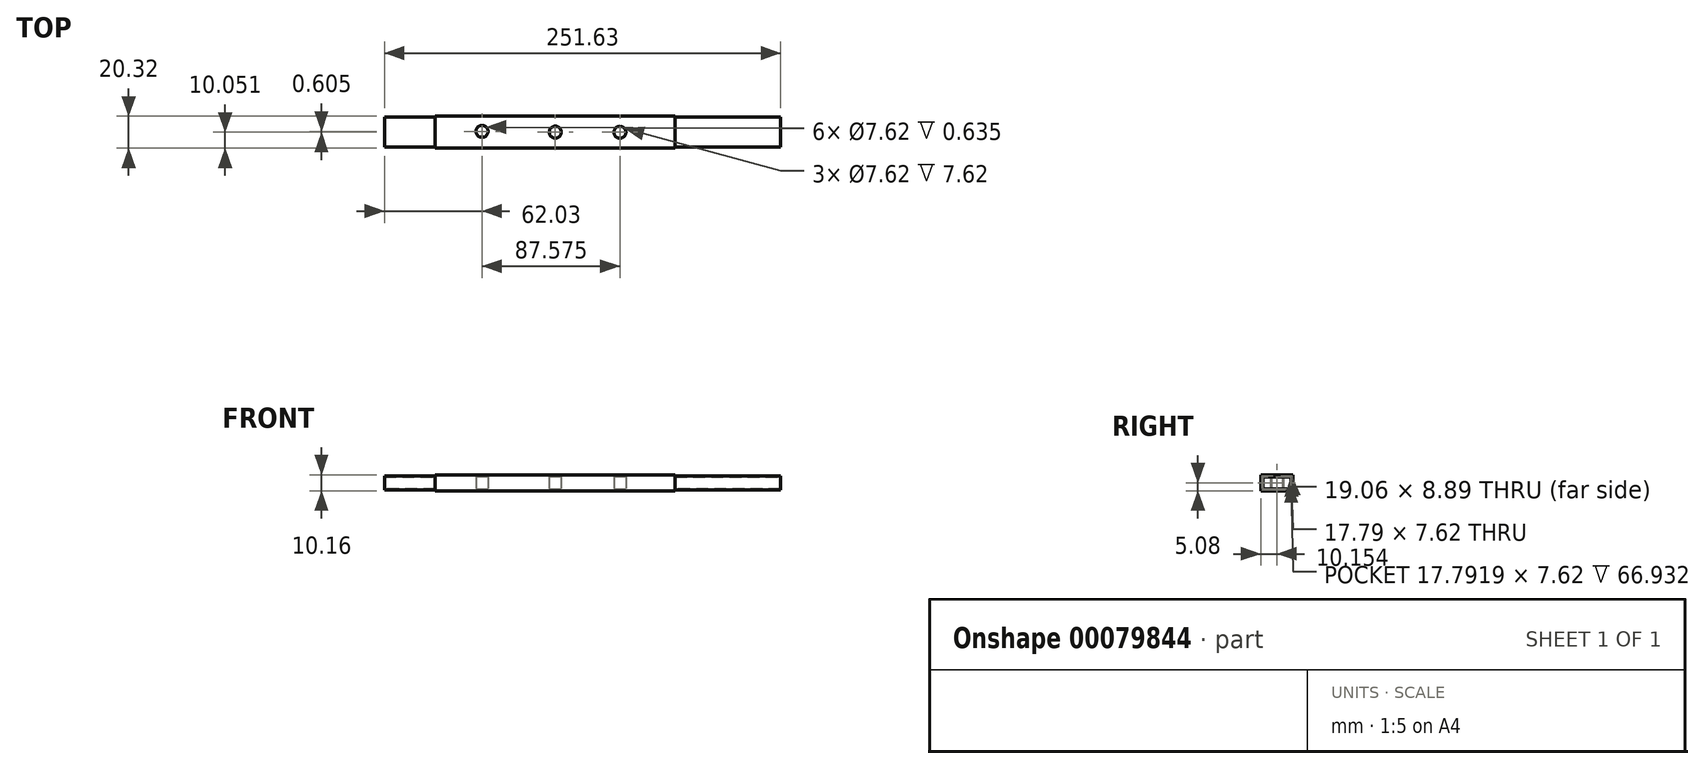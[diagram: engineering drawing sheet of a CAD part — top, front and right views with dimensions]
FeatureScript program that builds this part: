
annotation { "Feature Type Name" : "Feature", "Feature Type Description" : "" }
export const myFeature = defineFeature(function(context is Context, id is Id, definition is map)
    precondition{}
    {
        {
            var Q0;
            Q0=qCreatedBy(makeId("Top.planeOp"),FACE);
            var sketch = newSketch(context, id + "F0", { "sketchPlane" : qUnion([Q0])});
            skLineSegment(sketch, "E0.bottom", {"start": v(76.2, -10.16) * mm, "end": v(-76.2, -10.16) * mm});
            skLineSegment(sketch, "E0.top", {"start": v(76.2, 10.16) * mm, "end": v(-76.2, 10.16) * mm});
            skLineSegment(sketch, "E0.left", {"start": v(76.2, -10.16) * mm, "end": v(76.2, 10.16) * mm});
            skLineSegment(sketch, "E0.right", {"start": v(-76.2, -10.16) * mm, "end": v(-76.2, 10.16) * mm});
            skPoint(sketch, "E0.middle", {"position": v(0, 0) * mm});
            skCircle(sketch, "E1", {"center": v(0, 0) * mm, "radius": 3.81 * mm});
            skPoint(sketch, "E2.middle", {"position": v(-46.47, 0.5) * mm});
            skCircle(sketch, "E3", {"center": v(-46.47, 0.5) * mm, "radius": 3.81 * mm});
            skPoint(sketch, "E4.middle", {"position": v(41.1, -0.1) * mm});
            skCircle(sketch, "E5", {"center": v(41.1, -0.1) * mm, "radius": 3.81 * mm});
            skSolve(sketch);
        }
        {
            var Q0;
            Q0=makeQuery(id+"F0.imprint","IMPRINT",FACE,{"disambiguationData":[TD([[makeQuery(id+"F0.imprint","IMPRINT",EDGE,{"derivedFrom":sQuery(id+"F0.wireOp",EDGE,"E0.bottom")}),-1.0]])]});
            var Q1;
            Q1 = qSketchRegion(id + "F2", true);
            extrude(context, id + "F1", {"entities" : qUnion([Q0, Q1]), "depth" : 10.16 * mm});
        }
        {
            var Q0;
            Q0=makeQuery(id+"F1.opExtrude","SWEPT_FACE",FACE,{"disambiguationData":[OSD([sQuery(id+"F0.wireOp",EDGE,"E0.left")])]});
            var sketch = newSketch(context, id + "F2", { "sketchPlane" : qUnion([Q0])});
            skLineSegment(sketch, "E6.bottom", {"start": v(-9.54, 9.53) * mm, "end": v(9.53, 9.53) * mm});
            skLineSegment(sketch, "E6.top", {"start": v(-9.54, 0.64) * mm, "end": v(9.53, 0.64) * mm});
            skLineSegment(sketch, "E6.left", {"start": v(-9.54, 9.53) * mm, "end": v(-9.54, 0.64) * mm});
            skLineSegment(sketch, "E6.right", {"start": v(9.53, 9.53) * mm, "end": v(9.53, 0.64) * mm});
            skSolve(sketch);
        }
        {
            var Q0;
            Q0=sQuery(id+"F2.wireOp",EDGE,"E6.left");
            var Q1;
            Q1=sQuery(id+"F2.wireOp",EDGE,"E6.bottom");
            var Q2;
            Q2=sQuery(id+"F2.wireOp",EDGE,"E6.top");
            var Q3;
            Q3=sQuery(id+"F2.wireOp",EDGE,"E6.right");
            extrude(context, id + "F3", {"bodyType" : ToolBodyType.SURFACE, "surfaceEntities" : qUnion([Q0, Q1, Q2, Q3]), "depth" : 66.93 * mm, "hasSecondDirection" : true, "secondDirectionOppositeDirection" : true, "secondDirectionDepth" : 184.7 * mm});
        }
        {
            var Q0;
            Q0=makeQuery(id+"F3.opExtrude","SWEPT_FACE",FACE,{"disambiguationData":[OSD([sQuery(id+"F2.wireOp",EDGE,"E6.right")])]});
            extrude(context, id + "F4", {"entities" : qUnion([Q0]), "oppositeDirection" : true, "depth" : 0.64 * mm});
        }
        {
            var Q0;
            Q0=makeQuery(id+"F3.opExtrude","SWEPT_FACE",FACE,{"disambiguationData":[OSD([sQuery(id+"F2.wireOp",EDGE,"E6.bottom")])]});
            extrude(context, id + "F5", {"entities" : qUnion([Q0]), "operationType" : NewBodyOperationType.ADD, "oppositeDirection" : true, "depth" : 0.64 * mm});
        }
        {
            var Q0;
            Q0=makeQuery(id+"F3.opExtrude","SWEPT_FACE",FACE,{"disambiguationData":[OSD([sQuery(id+"F2.wireOp",EDGE,"E6.left")])]});
            extrude(context, id + "F6", {"entities" : qUnion([Q0]), "operationType" : NewBodyOperationType.ADD, "oppositeDirection" : true, "depth" : 0.64 * mm});
        }
        {
            var Q0;
            Q0=makeQuery(id+"F3.opExtrude","SWEPT_FACE",FACE,{"disambiguationData":[OSD([sQuery(id+"F2.wireOp",EDGE,"E6.top")])]});
            extrude(context, id + "F7", {"entities" : qUnion([Q0]), "operationType" : NewBodyOperationType.ADD, "oppositeDirection" : true, "depth" : 0.64 * mm});
        }
    });
